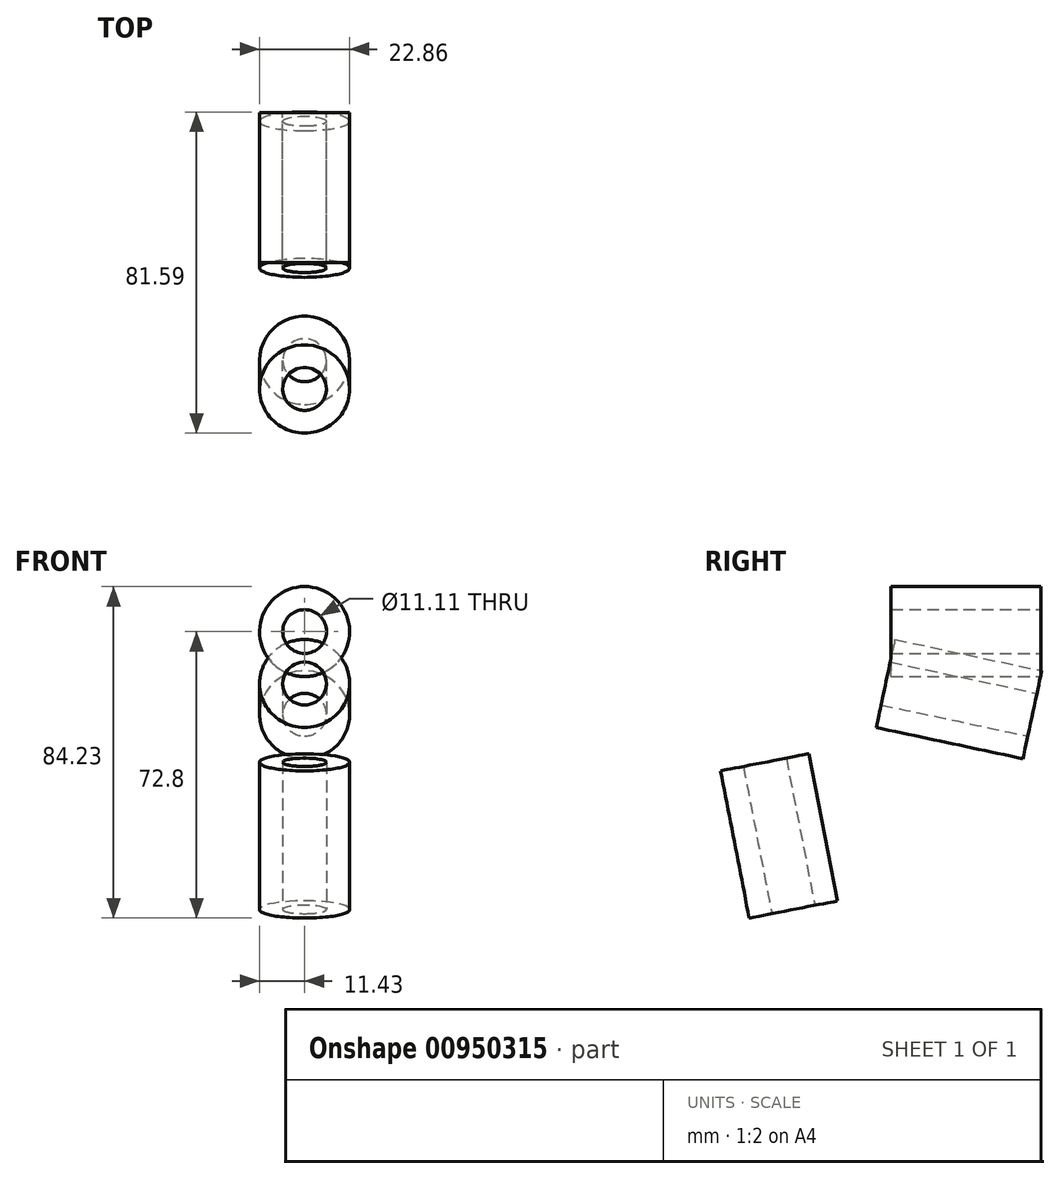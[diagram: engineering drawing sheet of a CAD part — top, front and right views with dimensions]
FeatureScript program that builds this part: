
annotation { "Feature Type Name" : "Feature", "Feature Type Description" : "" }
export const myFeature = defineFeature(function(context is Context, id is Id, definition is map)
    precondition{}
    {
        {
            var Q0;
            Q0=qCreatedBy(makeId("Front.planeOp"),FACE);
            var sketch = newSketch(context, id + "F0", { "sketchPlane" : qUnion([Q0])});
            skCircle(sketch, "E0", {"center": v(0, 0) * mm, "radius": 5.56 * mm});
            skCircle(sketch, "E1", {"center": v(0, 0) * mm, "radius": 11.43 * mm});
            skSolve(sketch);
        }
        {
            var Q0;
            Q0=makeQuery(id+"F0.imprint","IMPRINT",FACE,{"disambiguationData":[TD([[makeQuery(id+"F0.imprint","IMPRINT",EDGE,{"derivedFrom":sQuery(id+"F0.wireOp",EDGE,"E0")}),-1.0]])]});
            extrude(context, id + "F1", {"entities" : qUnion([Q0]), "depth" : 38.1 * mm, "offsetDistance" : 25.4 * mm});
        }
        {
            var Q0;
            Q0=qCreatedBy(makeId("Top.planeOp"),FACE);
            var sketch = newSketch(context, id + "F2", { "sketchPlane" : qUnion([Q0])});
            skLineSegment(sketch, "E2", {"start": v(46.53, -101.6) * mm, "end": v(-51.6, -101.6) * mm});
            skLineSegment(sketch, "E3", {"start": v(39.01, -69.97) * mm, "end": v(-47.56, -69.97) * mm});
            skSolve(sketch);
        }
        {
            var Q0;
            Q0=makeQuery(id+"F1.opExtrude","SWEPT_BODY",BODY,{"disambiguationData":[OSD([sQuery(id+"F0.wireOp",EDGE,"E0"),sQuery(id+"F0.wireOp",EDGE,"E1")])]});
            var Q1;
            Q1=sQuery(id+"F2.wireOp",EDGE,"E2");
            circularPattern(context, id + "F3", {"entities" : qUnion([Q0]), "axis" : qUnion([Q1]), "angle" : 12 * degree, "instanceCount" : 2, "equalSpace" : true});
        }
        {
            var Q0;
            Q0=makeQuery(id+"F3.opPattern","COPY",BODY,{"derivedFrom":makeQuery(id+"F1.opExtrude","SWEPT_BODY",BODY,{"disambiguationData":[OSD([sQuery(id+"F0.wireOp",EDGE,"E0"),sQuery(id+"F0.wireOp",EDGE,"E1")])]}),"instanceName":"1"});
            var Q1;
            Q1=sQuery(id+"F2.wireOp",EDGE,"E3");
            circularPattern(context, id + "F4", {"entities" : qUnion([Q0]), "axis" : qUnion([Q1]), "angle" : 67 * degree, "instanceCount" : 2, "equalSpace" : true});
        }
    });
